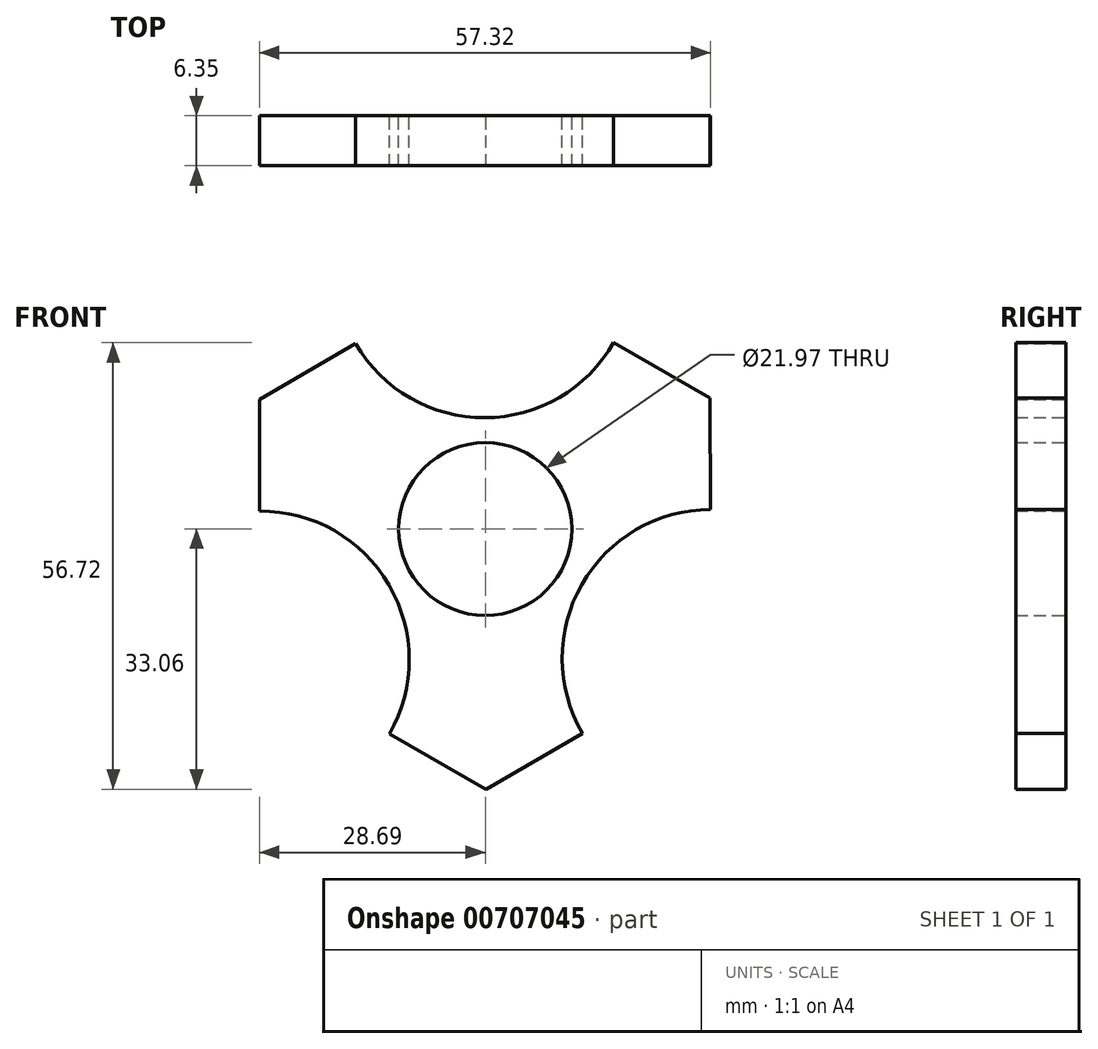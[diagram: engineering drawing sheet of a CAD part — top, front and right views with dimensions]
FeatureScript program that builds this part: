
annotation { "Feature Type Name" : "Feature", "Feature Type Description" : "" }
export const myFeature = defineFeature(function(context is Context, id is Id, definition is map)
    precondition{}
    {
        {
            var Q0;
            Q0=qCreatedBy(makeId("Front.planeOp"),FACE);
            var sketch = newSketch(context, id + "F0", { "sketchPlane" : qUnion([Q0])});
            skCircle(sketch, "E0.cCircle", {"center": v(0, 0) * mm, "radius": 28.63 * mm, "construction": true});
            skLineSegment(sketch, "E0.0", {"start": v(-0.12, 33.06) * mm, "end": v(28.58, 16.63) * mm});
            skLineSegment(sketch, "E0.1", {"start": v(28.58, 16.63) * mm, "end": v(28.7, -16.43) * mm});
            skLineSegment(sketch, "E0.2", {"start": v(28.7, -16.43) * mm, "end": v(0.12, -33.06) * mm});
            skLineSegment(sketch, "E0.3", {"start": v(0.12, -33.06) * mm, "end": v(-28.58, -16.63) * mm});
            skLineSegment(sketch, "E0.4", {"start": v(-28.58, -16.63) * mm, "end": v(-28.7, 16.43) * mm});
            skLineSegment(sketch, "E0.5", {"start": v(-28.7, 16.43) * mm, "end": v(-0.12, 33.06) * mm});
            skPoint(sketch, "E0.0.midPoint", {"position": v(14.23, 24.85) * mm});
            skCircle(sketch, "E1", {"center": v(0, 0) * mm, "radius": 10.99 * mm});
            skCircle(sketch, "E2", {"center": v(-0.12, 33.06) * mm, "radius": 18.92 * mm});
            skCircle(sketch, "E3", {"center": v(-28.58, -16.63) * mm, "radius": 18.92 * mm});
            skCircle(sketch, "E4", {"center": v(28.7, -16.43) * mm, "radius": 18.92 * mm});
            skSolve(sketch);
        }
        {
            var Q0;
            Q0=makeQuery(id+"F0.imprint","IMPRINT",FACE,{"disambiguationData":[TD([[makeQuery(id+"F0.imprint","IMPRINT",EDGE,{"derivedFrom":sQuery(id+"F0.wireOp",EDGE,"E1")}),-1.0]])]});
            extrude(context, id + "F1", {"entities" : qUnion([Q0]), "depth" : 6.35 * mm, "offsetDistance" : 25.4 * mm});
        }
    });
